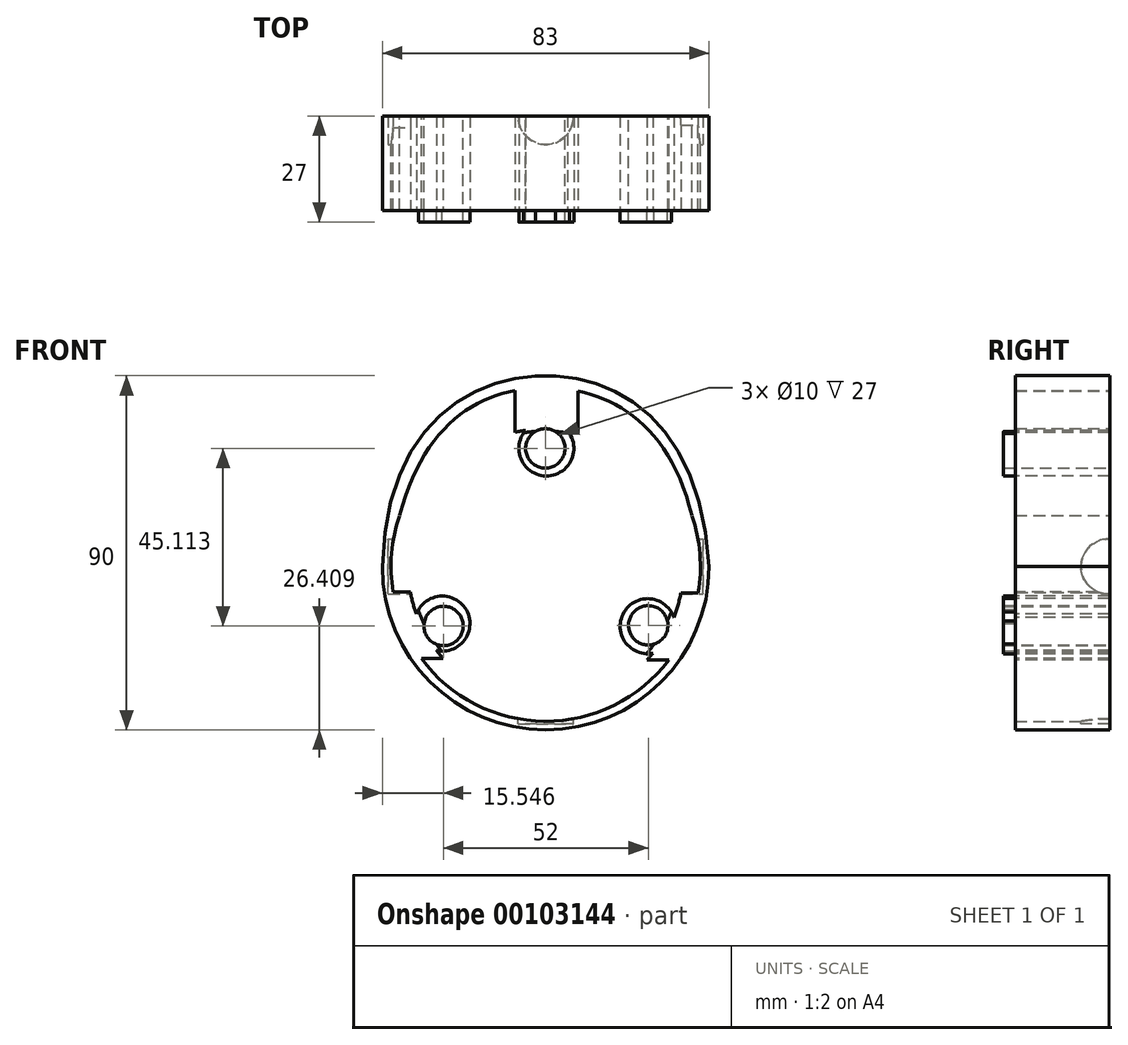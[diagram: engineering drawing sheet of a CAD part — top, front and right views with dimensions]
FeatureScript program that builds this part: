
annotation { "Feature Type Name" : "Feature", "Feature Type Description" : "" }
export const myFeature = defineFeature(function(context is Context, id is Id, definition is map)
    precondition{}
    {
        {
            var Q0;
            Q0=qCreatedBy(makeId("Front.planeOp"),FACE);
            var sketch = newSketch(context, id + "F0", { "sketchPlane" : qUnion([Q0])});
            skArc(sketch, "E0", {"start": v(-41.5, 0) * mm, "mid": v(0, -41.5) * mm, "end": v(41.5, 0) * mm});
            skLineSegment(sketch, "E1", {"start": v(0, -41.5) * mm, "end": v(0, 48.5) * mm, "construction": true});
            skFitSpline(sketch, "E2", {"points": [v(-41.5, 0) * mm, v(0, 48.5) * mm, v(41.5, 0) * mm], "startDerivative": vector(5.1, 210.5) * mm, "endDerivative": vector(12.98, -210.5) * mm});
            skLineSegment(sketch, "E3", {"start": v(-50.23, 35.08) * mm, "end": v(53.3, 35.08) * mm, "construction": true});
            skSolve(sketch);
        }
        {
            var Q0;
            Q0=makeQuery(id+"F0.imprint","IMPRINT",FACE,{"disambiguationData":[TD([[makeQuery(id+"F0.imprint","IMPRINT",EDGE,{"derivedFrom":sQuery(id+"F0.wireOp",EDGE,"E0")}),1.0]])]});
            extrude(context, id + "F1", {"entities" : qUnion([Q0]), "depth" : 27 * mm, "symmetric" : true});
        }
        {
            var Q0;
            Q0=makeQuery(id+"F1.opExtrude","CAP_FACE",FACE,{"disambiguationData":[OSD([sQuery(id+"F0.wireOp",EDGE,"E0"),sQuery(id+"F0.wireOp",EDGE,"E2")])],"isStart":false});
            var sketch = newSketch(context, id + "F2", { "sketchPlane" : qUnion([Q0])});
            skCircle(sketch, "E4", {"center": v(0, 0) * mm, "radius": 35 * mm});
            skCircle(sketch, "E5", {"center": v(0.17, 30.02) * mm, "radius": 7 * mm});
            skCircle(sketch, "E6", {"center": v(25.91, -15.16) * mm, "radius": 7 * mm});
            skCircle(sketch, "E7", {"center": v(-26.27, -14.5) * mm, "radius": 7 * mm});
            skSolve(sketch);
        }
        {
            var Q0;
            Q0=makeQuery(id+"F2.imprint","IMPRINT",FACE,{"disambiguationData":[TD([[makeQuery(id+"F2.imprint","IMPRINT",EDGE,{"derivedFrom":sQuery(id+"F2.wireOp",EDGE,"E4")}),1.0]])]});
            extrude(context, id + "F3", {"entities" : qUnion([Q0]), "operationType" : NewBodyOperationType.REMOVE, "oppositeDirection" : true, "depth" : 30 * mm});
        }
        {
            var Q0;
            Q0=makeQuery(id+"F1.opExtrude","CAP_FACE",FACE,{"disambiguationData":[OSD([sQuery(id+"F0.wireOp",EDGE,"E0"),sQuery(id+"F0.wireOp",EDGE,"E2")])],"isStart":false});
            var sketch = newSketch(context, id + "F4", { "sketchPlane" : qUnion([Q0])});
            skLineSegment(sketch, "E8.bottom", {"start": v(47.27, -50.56) * mm, "end": v(-48.18, -50.56) * mm});
            skLineSegment(sketch, "E8.top", {"start": v(47.27, 51.1) * mm, "end": v(-48.18, 51.1) * mm});
            skLineSegment(sketch, "E8.left", {"start": v(47.27, -50.56) * mm, "end": v(47.27, 51.1) * mm});
            skLineSegment(sketch, "E8.right", {"start": v(-48.18, -50.56) * mm, "end": v(-48.18, 51.1) * mm});
            skPoint(sketch, "E8.middle", {"position": v(-0.45, 0.27) * mm});
            skCircle(sketch, "E9", {"center": v(-0.14, 0.3) * mm, "radius": 34.14 * mm});
            skSolve(sketch);
        }
        {
            var Q0;
            Q0=makeQuery(id+"F4.imprint","IMPRINT",FACE,{"disambiguationData":[TD([[makeQuery(id+"F4.imprint","IMPRINT",EDGE,{"derivedFrom":makeQuery(id+"F1.opExtrude","CAP_EDGE",EDGE,{"disambiguationData":[OSD([sQuery(id+"F0.wireOp",EDGE,"E0")])],"isStart":false})}),1.0]])]});
            extrude(context, id + "F5", {"entities" : qUnion([Q0]), "operationType" : NewBodyOperationType.REMOVE, "oppositeDirection" : true, "depth" : 3 * mm});
        }
        {
            var Q0;
            Q0=makeQuery(id+"F1.opExtrude","CAP_FACE",FACE,{"disambiguationData":[OSD([sQuery(id+"F0.wireOp",EDGE,"E0"),sQuery(id+"F0.wireOp",EDGE,"E2")])],"isStart":true});
            var sketch = newSketch(context, id + "F6", { "sketchPlane" : qUnion([Q0])});
            skCircle(sketch, "E10.cCircle", {"center": v(0, 0) * mm, "radius": 30.02 * mm, "construction": true});
            skLineSegment(sketch, "E10.0", {"start": v(25.95, -15.1) * mm, "end": v(-26.05, -14.93) * mm});
            skLineSegment(sketch, "E10.1", {"start": v(-26.05, -14.93) * mm, "end": v(0.1, 30.02) * mm});
            skLineSegment(sketch, "E10.2", {"start": v(0.1, 30.02) * mm, "end": v(25.95, -15.1) * mm});
            skSolve(sketch);
        }
        {
            var Q0;
            Q0=sQuery(id+"F6.wireOp",VERTEX,"E10.2.start");
            var Q1;
            Q1=sQuery(id+"F6.wireOp",VERTEX,"E10.1.start");
            var Q2;
            Q2=sQuery(id+"F6.wireOp",VERTEX,"E10.2.end");
            var Q3;
            Q3=makeQuery(id+"F1.opExtrude","SWEPT_BODY",BODY,{"disambiguationData":[OSD([sQuery(id+"F0.wireOp",EDGE,"E0"),sQuery(id+"F0.wireOp",EDGE,"E2")])]});
            hole(context, id + "F7", {"style" : HoleStyle.SIMPLE, "endStyle" : HoleEndStyle.THROUGH, "holeDiameter" : 10 * mm, "locations" : qUnion([Q0, Q1, Q2]), "scope" : qUnion([Q3]), "isTappedThrough" : true});
        }
        {
            var Q0;
            Q0=qCreatedBy(makeId("Top.planeOp"),FACE);
            var sketch = newSketch(context, id + "F8", { "sketchPlane" : qUnion([Q0])});
            skCircle(sketch, "E11", {"center": v(0, 13.22) * mm, "radius": 7 * mm});
            skSolve(sketch);
        }
        {
            var Q0;
            Q0=makeQuery(id+"F8.imprint","IMPRINT",FACE,{"disambiguationData":[TD([[makeQuery(id+"F8.imprint","IMPRINT",EDGE,{"derivedFrom":sQuery(id+"F8.wireOp",EDGE,"E11")}),1.0]])]});
            extrude(context, id + "F9", {"entities" : qUnion([Q0]), "operationType" : NewBodyOperationType.REMOVE, "oppositeDirection" : true, "depth" : 40 * mm});
        }
        {
            var Q0;
            Q0=qCreatedBy(makeId("Right.planeOp"),FACE);
            var sketch = newSketch(context, id + "F10", { "sketchPlane" : qUnion([Q0])});
            skCircle(sketch, "E12", {"center": v(13.17, 0) * mm, "radius": 7 * mm});
            skSolve(sketch);
        }
        {
            var Q0;
            Q0=makeQuery(id+"F10.imprint","IMPRINT",FACE,{"disambiguationData":[TD([[makeQuery(id+"F10.imprint","IMPRINT",EDGE,{"derivedFrom":sQuery(id+"F10.wireOp",EDGE,"E12")}),1.0]])]});
            extrude(context, id + "F11", {"entities" : qUnion([Q0]), "operationType" : NewBodyOperationType.REMOVE, "oppositeDirection" : true, "depth" : 80 * mm, "symmetric" : true});
        }
        {
            var Q0;
            Q0=qCreatedBy(makeId("Front.planeOp"),FACE);
            var sketch = newSketch(context, id + "F12", { "sketchPlane" : qUnion([Q0])});
            skArc(sketch, "E13", {"start": v(-37.11, 12.92) * mm, "mid": v(-39.15, 3.33) * mm, "end": v(-38.76, -6.46) * mm});
            skLineSegment(sketch, "E14", {"start": v(-54.8, 12.92) * mm, "end": v(68.26, 12.92) * mm, "construction": true});
            skFitSpline(sketch, "E15", {"points": [v(-37.11, 12.92) * mm, v(0, 45.42) * mm, v(37.11, 12.92) * mm], "startDerivative": vector(37.66, 147.05) * mm, "endDerivative": vector(34.52, -145.24) * mm});
            skLineSegment(sketch, "E16.bottom", {"start": v(8.17, 44.58) * mm, "end": v(8.17, 44.58) * mm});
            skLineSegment(sketch, "E16.top", {"start": v(-7.79, 21.73) * mm, "end": v(8.17, 21.73) * mm});
            skLineSegment(sketch, "E16.left", {"start": v(-7.79, 44.72) * mm, "end": v(-7.79, 21.73) * mm});
            skLineSegment(sketch, "E16.right", {"start": v(8.17, 44.58) * mm, "end": v(8.17, 21.73) * mm});
            skLineSegment(sketch, "E17.bottom", {"start": v(38.72, -6.69) * mm, "end": v(17.65, -6.69) * mm});
            skLineSegment(sketch, "E17.top", {"start": v(31.29, -23.77) * mm, "end": v(17.65, -23.77) * mm});
            skLineSegment(sketch, "E17.right", {"start": v(17.65, -6.69) * mm, "end": v(17.65, -23.77) * mm});
            skArc(sketch, "E18.trimOffspring", {"start": v(38.72, -6.69) * mm, "mid": v(39.16, 3.22) * mm, "end": v(37.11, 12.92) * mm});
            skLineSegment(sketch, "E19.bottom", {"start": v(-38.76, -6.46) * mm, "end": v(-17.48, -6.46) * mm});
            skLineSegment(sketch, "E19.top", {"start": v(-31.6, -23.35) * mm, "end": v(-17.48, -23.35) * mm});
            skLineSegment(sketch, "E19.right", {"start": v(-17.48, -6.46) * mm, "end": v(-17.48, -23.35) * mm});
            skArc(sketch, "E20.trimOffspring", {"start": v(-31.6, -23.35) * mm, "mid": v(-0.26, -39.3) * mm, "end": v(31.29, -23.77) * mm});
            skSolve(sketch);
        }
        {
            var Q0;
            Q0=makeQuery(id+"F12.imprint","IMPRINT",FACE,{"disambiguationData":[TD([[makeQuery(id+"F12.imprint","IMPRINT",EDGE,{"derivedFrom":sQuery(id+"F12.wireOp",EDGE,"E13")}),1.0]])]});
            extrude(context, id + "F13", {"entities" : qUnion([Q0]), "operationType" : NewBodyOperationType.REMOVE, "depth" : 90 * mm, "symmetric" : true});
        }
    });
